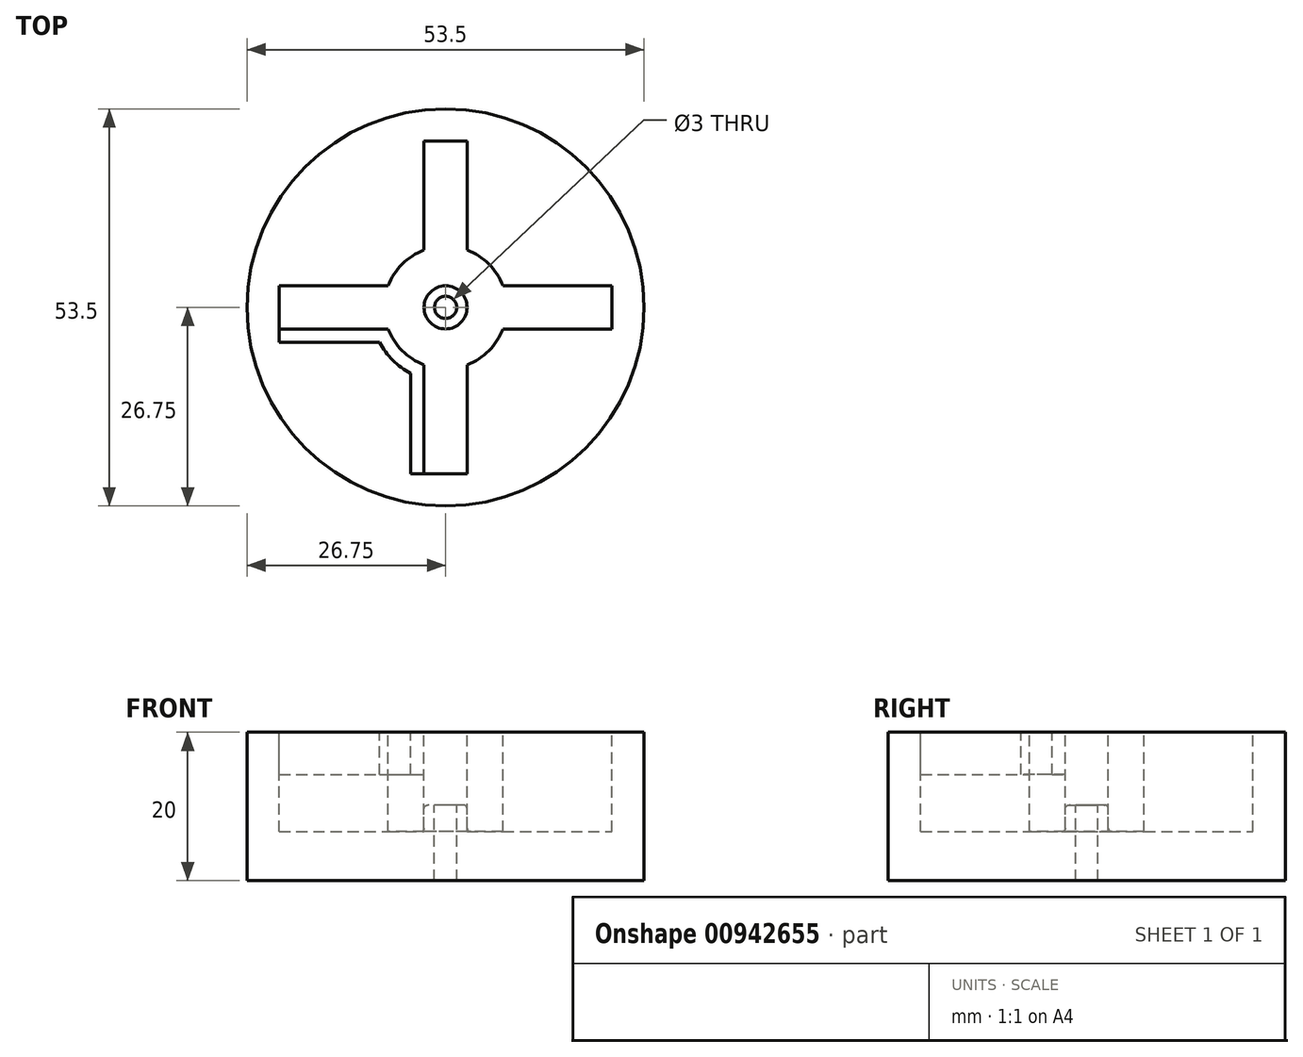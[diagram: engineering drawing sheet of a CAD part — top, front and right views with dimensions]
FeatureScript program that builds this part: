
annotation { "Feature Type Name" : "Feature", "Feature Type Description" : "" }
export const myFeature = defineFeature(function(context is Context, id is Id, definition is map)
    precondition{}
    {
        {
            var Q0;
            Q0=qCreatedBy(makeId("Right.planeOp"),FACE);
            var sketch = newSketch(context, id + "F0", { "sketchPlane" : qUnion([Q0])});
            skLineSegment(sketch, "E0", {"start": v(0, 35.9) * mm, "end": v(0, -35.2) * mm, "construction": true});
            skLineSegment(sketch, "E1", {"start": v(1.5, 0) * mm, "end": v(1.5, 10.2) * mm});
            skLineSegment(sketch, "E2", {"start": v(1.5, 10.2) * mm, "end": v(4.13, 10.2) * mm});
            skLineSegment(sketch, "E3", {"start": v(4.13, 10.2) * mm, "end": v(4.12, 20) * mm});
            skLineSegment(sketch, "E4", {"start": v(4.12, 20) * mm, "end": v(26.75, 20) * mm});
            skLineSegment(sketch, "E5", {"start": v(26.75, 20) * mm, "end": v(26.75, 0) * mm});
            skLineSegment(sketch, "E6", {"start": v(26.75, 0) * mm, "end": v(1.5, 0) * mm});
            skSolve(sketch);
        }
        {
            var Q0;
            Q0 = qSketchRegion(id + "F0", true);
            var Q1;
            Q1=sQuery(id+"F0.wireOp",EDGE,"E0");
            revolve(context, id + "F1", {"surfaceOperationType" : NewSurfaceOperationType.NEW, "entities" : qUnion([Q0]), "axis" : qUnion([Q1]), "revolveType" : RevolveType.FULL});
        }
        {
            var Q0;
            Q0=makeQuery(id+"F1.opRevolve","SWEPT_FACE",FACE,{"disambiguationData":[OSD([sQuery(id+"F0.wireOp",EDGE,"E4")])]});
            var sketch = newSketch(context, id + "F2", { "sketchPlane" : qUnion([Q0])});
            skLineSegment(sketch, "E7.bottom", {"start": v(-22.4, -2.9) * mm, "end": v(22.4, -2.9) * mm});
            skLineSegment(sketch, "E7.top", {"start": v(-22.4, 2.9) * mm, "end": v(22.4, 2.9) * mm});
            skLineSegment(sketch, "E7.left", {"start": v(-22.4, -2.9) * mm, "end": v(-22.4, 2.9) * mm});
            skLineSegment(sketch, "E7.right", {"start": v(22.4, -2.9) * mm, "end": v(22.4, 2.9) * mm});
            skPoint(sketch, "E7.middle", {"position": v(0, 0) * mm});
            skLineSegment(sketch, "E8.bottom", {"start": v(2.9, -22.4) * mm, "end": v(-2.9, -22.4) * mm});
            skLineSegment(sketch, "E8.top", {"start": v(2.9, 22.4) * mm, "end": v(-2.9, 22.4) * mm});
            skLineSegment(sketch, "E8.left", {"start": v(2.9, -22.4) * mm, "end": v(2.9, 22.4) * mm});
            skLineSegment(sketch, "E8.right", {"start": v(-2.9, -22.4) * mm, "end": v(-2.9, 22.4) * mm});
            skCircle(sketch, "E9", {"center": v(0, 0) * mm, "radius": 8.25 * mm});
            skSolve(sketch);
        }
        {
            var Q0;
            Q0 = qSketchRegion(id + "F2", true);
            extrude(context, id + "F3", {"entities" : qUnion([Q0]), "operationType" : NewBodyOperationType.REMOVE, "oppositeDirection" : true, "depth" : 13.4 * mm, "offsetDistance" : 25 * mm});
        }
        {
            var Q0;
            Q0=makeQuery(id+"F1.opRevolve","SWEPT_FACE",FACE,{"disambiguationData":[OSD([sQuery(id+"F0.wireOp",EDGE,"E4")])]});
            var sketch = newSketch(context, id + "F4", { "sketchPlane" : qUnion([Q0])});
            skLineSegment(sketch, "E10.0", {"start": v(-4.7, -22.4) * mm, "end": v(-4.7, -8.88) * mm});
            skArc(sketch, "E10.1", {"start": v(-8.88, -4.7) * mm, "mid": v(-7.1, -7.1) * mm, "end": v(-4.7, -8.88) * mm});
            skLineSegment(sketch, "E10.2", {"start": v(-22.4, -4.7) * mm, "end": v(-8.88, -4.7) * mm});
            skLineSegment(sketch, "E11", {"start": v(-22.4, -4.7) * mm, "end": v(-22.4, -2.9) * mm});
            skLineSegment(sketch, "E12", {"start": v(-4.7, -22.4) * mm, "end": v(-2.9, -22.4) * mm});
            skLineSegment(sketch, "E13", {"start": v(-22.4, -2.9) * mm, "end": v(-7.72, -2.9) * mm});
            skLineSegment(sketch, "E14", {"start": v(-2.9, -22.4) * mm, "end": v(-2.9, -7.72) * mm});
            skArc(sketch, "E15", {"start": v(-7.72, -2.9) * mm, "mid": v(-5.83, -5.83) * mm, "end": v(-2.9, -7.72) * mm});
            skSolve(sketch);
        }
        {
            var Q0;
            Q0=makeQuery(id+"F3.boolean.opBoolean","COPY",EDGE,{"derivedFrom":makeQuery(id+"F3.opExtrude","SWEPT_EDGE",EDGE,{"disambiguationData":[OSD([sQuery(id+"F2.wireOp",EDGE,"E7.top"),sQuery(id+"F2.wireOp",EDGE,"E8.left")])]})});
            var Q1;
            Q1=makeQuery(id+"F3.boolean.opBoolean","COPY",EDGE,{"derivedFrom":makeQuery(id+"F3.opExtrude","SWEPT_EDGE",EDGE,{"disambiguationData":[OSD([sQuery(id+"F2.wireOp",EDGE,"E7.bottom"),sQuery(id+"F2.wireOp",EDGE,"E8.right")])]})});
            var Q2;
            Q2=makeQuery(id+"F3.boolean.opBoolean","COPY",EDGE,{"derivedFrom":makeQuery(id+"F3.opExtrude","SWEPT_EDGE",EDGE,{"disambiguationData":[OSD([sQuery(id+"F2.wireOp",EDGE,"E7.top"),sQuery(id+"F2.wireOp",EDGE,"E8.right")])]})});
            var Q3;
            Q3=makeQuery(id+"F3.boolean.opBoolean","COPY",EDGE,{"derivedFrom":makeQuery(id+"F3.opExtrude","SWEPT_EDGE",EDGE,{"disambiguationData":[OSD([sQuery(id+"F2.wireOp",EDGE,"E7.bottom"),sQuery(id+"F2.wireOp",EDGE,"E8.left")])]})});
            fillet(context, id + "F5", {"entities" : qUnion([Q0, Q1, Q2, Q3]), "radius" : 2.9 * mm, "tangentPropagation" : true, "allowEdgeOverflow" : false});
        }
        {
            var Q0;
            {var subQ0=sQuery(id+"F2.wireOp",EDGE,"E8.right");var subQ1=sQuery(id+"F2.wireOp",EDGE,"E7.bottom");Q0=makeQuery(id+"F5.opFillet","BLEND_EDGE",EDGE,{"blendedFrom":[makeQuery(id+"F3.boolean.opBoolean","COPY",EDGE,{"derivedFrom":makeQuery(id+"F3.opExtrude","SWEPT_EDGE",EDGE,{"disambiguationData":[OSD([subQ1,subQ0])]})}),makeQuery(id+"F3.boolean.opBoolean","COPY",FACE,{"derivedFrom":makeQuery(id+"F3.opExtrude","CAP_FACE",FACE,{"disambiguationData":[OSD([subQ1,sQuery(id+"F2.wireOp",EDGE,"E7.top"),sQuery(id+"F2.wireOp",EDGE,"E7.left"),sQuery(id+"F2.wireOp",EDGE,"E7.right"),sQuery(id+"F2.wireOp",EDGE,"E8.bottom"),sQuery(id+"F2.wireOp",EDGE,"E8.top"),sQuery(id+"F2.wireOp",EDGE,"E8.left"),subQ0,sQuery(id+"F2.wireOp",EDGE,"E9")])],"isStart":false})})],"blendedInto":[makeQuery(id+"F3.boolean.opBoolean","COPY",FACE,{"derivedFrom":makeQuery(id+"F3.opExtrude","CAP_FACE",FACE,{"disambiguationData":[OSD([subQ1,sQuery(id+"F2.wireOp",EDGE,"E7.top"),sQuery(id+"F2.wireOp",EDGE,"E7.left"),sQuery(id+"F2.wireOp",EDGE,"E7.right"),sQuery(id+"F2.wireOp",EDGE,"E8.bottom"),sQuery(id+"F2.wireOp",EDGE,"E8.top"),sQuery(id+"F2.wireOp",EDGE,"E8.left"),subQ0,sQuery(id+"F2.wireOp",EDGE,"E9")])],"isStart":false})})]});}
            var Q1;
            Q1=makeQuery(id+"F5.opFillet","BLEND_EDGE",EDGE,{"blendedFrom":[makeQuery(id+"F3.boolean.opBoolean","COPY",EDGE,{"derivedFrom":makeQuery(id+"F3.opExtrude","SWEPT_EDGE",EDGE,{"disambiguationData":[OSD([sQuery(id+"F2.wireOp",EDGE,"E7.bottom"),sQuery(id+"F2.wireOp",EDGE,"E8.right")])]})}),makeQuery(id+"F1.opRevolve","SWEPT_FACE",FACE,{"disambiguationData":[OSD([sQuery(id+"F0.wireOp",EDGE,"E2")])]})],"blendedInto":[makeQuery(id+"F1.opRevolve","SWEPT_FACE",FACE,{"disambiguationData":[OSD([sQuery(id+"F0.wireOp",EDGE,"E2")])]})]});
            fillet(context, id + "F6", {"entities" : qUnion([Q0, Q1]), "radius" : 0.5 * mm, "tangentPropagation" : true, "allowEdgeOverflow" : false});
        }
        {
            var Q0;
            Q0 = qSketchRegion(id + "F4", true);
            extrude(context, id + "F7", {"entities" : qUnion([Q0]), "operationType" : NewBodyOperationType.REMOVE, "oppositeDirection" : true, "depth" : 5.7 * mm, "offsetDistance" : 25 * mm});
        }
    });
